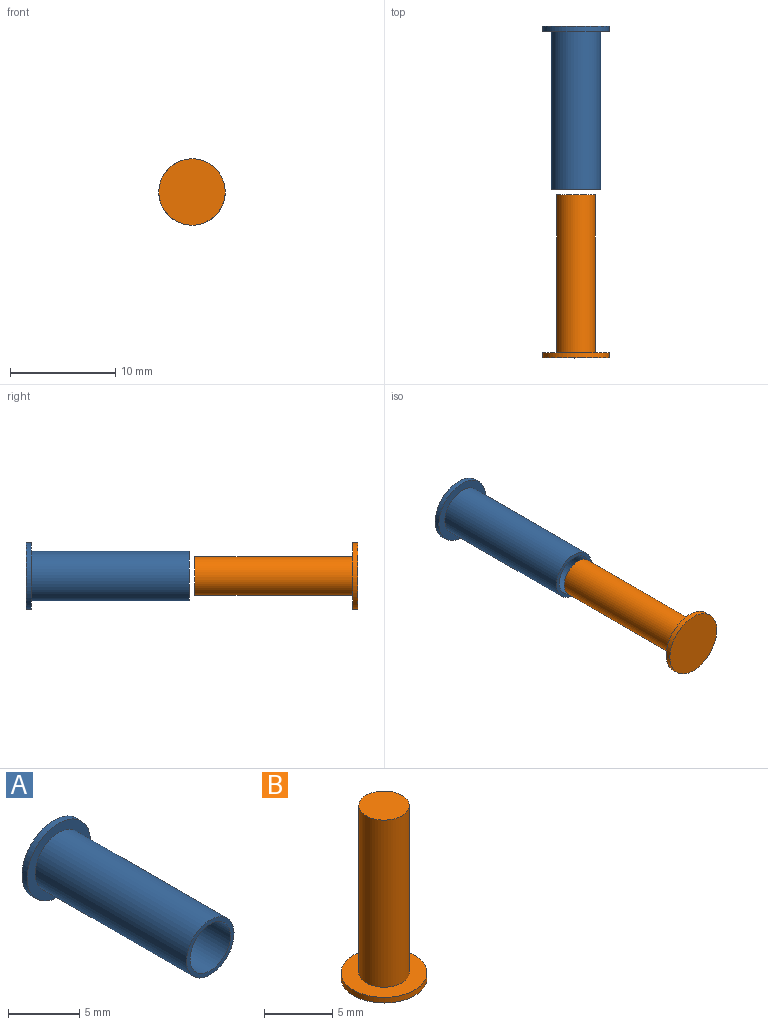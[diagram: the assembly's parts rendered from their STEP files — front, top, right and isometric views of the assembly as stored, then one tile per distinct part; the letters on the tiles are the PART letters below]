
ASSEMBLY  parts=2 mates=1
PART A: 7 faces, bbox 6.3x15.5x6.3 mm
  f0: cylinder r=3.15mm len=6.3mm, axis (0,1,0), area 9.9mm2, adj f1,f2
  f1: plane 6.3x6.3mm, normal (0,-1,0), area 13.8mm2, adj f0,f3
  f2: plane 6.3x6.3mm, normal (0,1,0), area 31.2mm2, adj f0
  f3: cylinder r=2.35mm len=15mm, axis (0,1,0), area 221.5mm2, adj f1,f4
  f4: plane 4.7x4.7mm, normal (0,-1,0), area 4.8mm2, adj f3,f5
  f5: cylinder r=2mm len=15mm, axis (0,-1,0), area 188.5mm2, adj f4,f6
  f6: plane 4x4mm, normal (0,-1,0), area 12.6mm2, adj f5
PART B: 5 faces, bbox 6.3x6.3x15.5 mm
  f0: cylinder r=3.15mm len=6.3mm, axis (0,0,-1), area 9.9mm2, adj f1,f2
  f1: plane 6.3x6.3mm, normal (0,0,1), area 20.4mm2, adj f0,f3
  f2: plane 6.3x6.3mm, normal (0,0,-1), area 31.2mm2, adj f0
  f3: cylinder r=1.85mm len=15mm, axis (0,0,-1), area 174.4mm2, adj f1,f4
  f4: plane 3.7x3.7mm, normal (0,0,1), area 10.8mm2, adj f3
PLACE A t=(-10.54,9.52,8.37)mm fixed
PLACE B rot(axis=(-1,0,0),90deg) t=(-10.54,-22,8.37)mm
MATE slider B.f3 <-> A.f3  axis (0,1,0) through (-10.54,-6.5,8.37)mm
